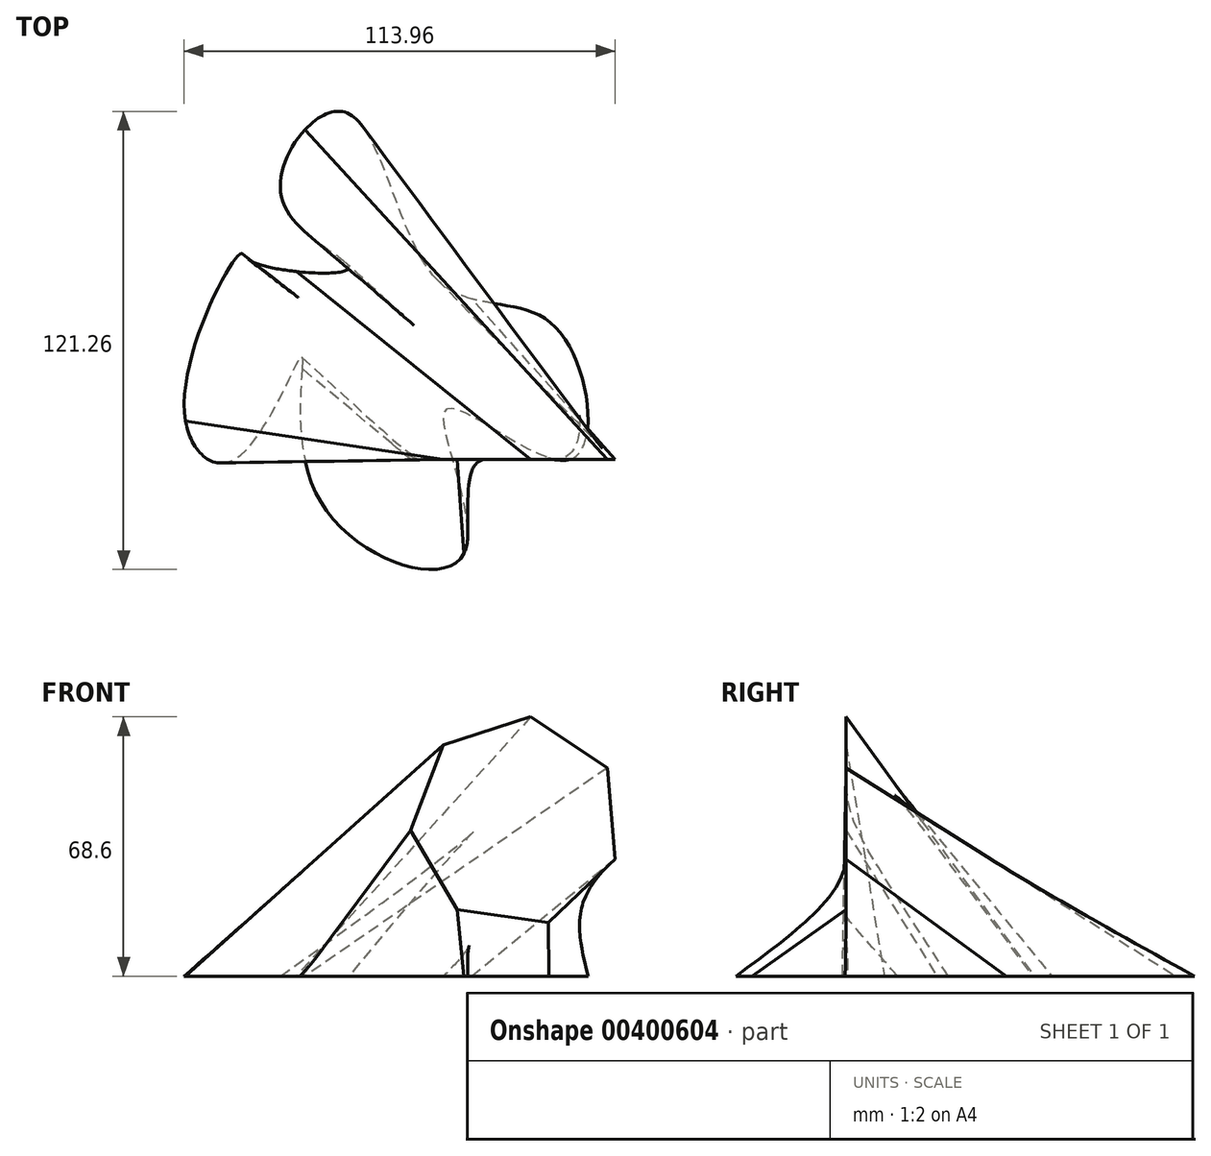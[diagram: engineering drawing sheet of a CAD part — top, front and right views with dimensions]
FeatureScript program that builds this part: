
annotation { "Feature Type Name" : "Feature", "Feature Type Description" : "" }
export const myFeature = defineFeature(function(context is Context, id is Id, definition is map)
    precondition{}
    {
        {
            var Q0;
            Q0=qCreatedBy(makeId("Front.planeOp"),FACE);
            var sketch = newSketch(context, id + "F0", { "sketchPlane" : qUnion([Q0])});
            skCircle(sketch, "E0.cCircle", {"center": v(26.79, 40.87) * mm, "radius": 25.23 * mm, "construction": true});
            skLineSegment(sketch, "E0.0", {"start": v(35.3, 14.18) * mm, "end": v(11.23, 17.58) * mm});
            skLineSegment(sketch, "E0.1", {"start": v(11.23, 17.58) * mm, "end": v(-1.12, 38.51) * mm});
            skLineSegment(sketch, "E0.2", {"start": v(-1.12, 38.51) * mm, "end": v(7.55, 61.22) * mm});
            skLineSegment(sketch, "E0.3", {"start": v(7.55, 61.22) * mm, "end": v(30.7, 68.6) * mm});
            skLineSegment(sketch, "E0.4", {"start": v(30.7, 68.6) * mm, "end": v(50.91, 55.1) * mm});
            skLineSegment(sketch, "E0.5", {"start": v(50.91, 55.1) * mm, "end": v(52.96, 30.88) * mm});
            skLineSegment(sketch, "E0.6", {"start": v(52.96, 30.88) * mm, "end": v(35.3, 14.18) * mm});
            skPoint(sketch, "E0.0.midPoint", {"position": v(23.26, 15.88) * mm});
            skSolve(sketch);
        }
        {
            var Q0;
            Q0=qCreatedBy(makeId("Top.planeOp"),FACE);
            var sketch = newSketch(context, id + "F1", { "sketchPlane" : qUnion([Q0])});
            skFitSpline(sketch, "E1", {"points": [v(-46.2, 54.4) * mm, v(-60.94, 12.75) * mm, v(-47.76, 0) * mm, v(-30.07, 27.05) * mm, v(-25.36, -10.41) * mm, v(12.98, -24.93) * mm, v(8.5, 13.37) * mm, v(41, 0) * mm, v(37.3, 34.93) * mm, v(6.19, 47.28) * mm, v(-18.93, 92) * mm, v(-35.03, 68.6) * mm, v(-17.53, 50.5) * mm, v(-43.36, 52.51) * mm, v(-46.2, 54.4) * mm]});
            skSolve(sketch);
        }
        {
            var Q0;
            Q0 = qSketchRegion(id + "F0", true);
            var Q1;
            Q1 = qSketchRegion(id + "F1", true);
            loft(context, id + "F2", {"sheetProfilesArray" : [{ "sheetProfileEntities" : qUnion([Q0]) }, { "sheetProfileEntities" : qUnion([Q1]) }]});
        }
    });
